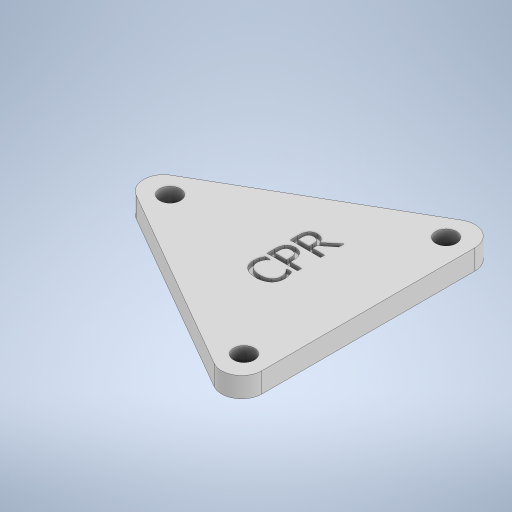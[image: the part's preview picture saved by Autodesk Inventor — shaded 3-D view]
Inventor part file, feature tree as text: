
AUTODESK INVENTOR PART (.ipt)
format: ipt  version: 2023 (Build 270158000, 158)  size: 339,968 bytes
history: native  units: mm
features: sketch x2, extrude x1, emboss x1
ambient origin geometry x8: Origin, YZ Plane, XZ Plane, XY Plane, X Axis, Y Axis, Z Axis, Center Point
bodies: Solid1 (feature_tree)
feature tree (4):
  extrude  "Extrusion1"  Depth=100.0mm
  emboss  "Emboss1"
  sketch  "Sketch1"  dims[d0=10.254mm d1=100.0mm]
  sketch  "Sketch2"  dims[d2=140.0mm d3=10.0mm d4=10.0mm d5=0.0mm d6=2.0mm d7=0.0mm]
